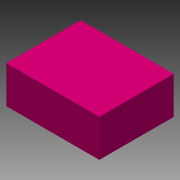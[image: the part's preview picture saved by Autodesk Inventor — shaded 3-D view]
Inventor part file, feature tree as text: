
AUTODESK INVENTOR PART (.ipt)
format: ipt  version: 2015 (Build 190159000, 159)  size: 82,944 bytes
history: native  units: mm
features: other x1, extrude x1, sketch x1
ambient origin geometry x8: Origin, YZ Plane, XZ Plane, XY Plane, X Axis, Y Axis, Z Axis, Center Point
bodies: Body1 (feature_tree)
feature tree (3):
  other  "ソリッド1"
  extrude  "押し出し1"  Depth=100.0mm
  sketch  "スケッチ1"
